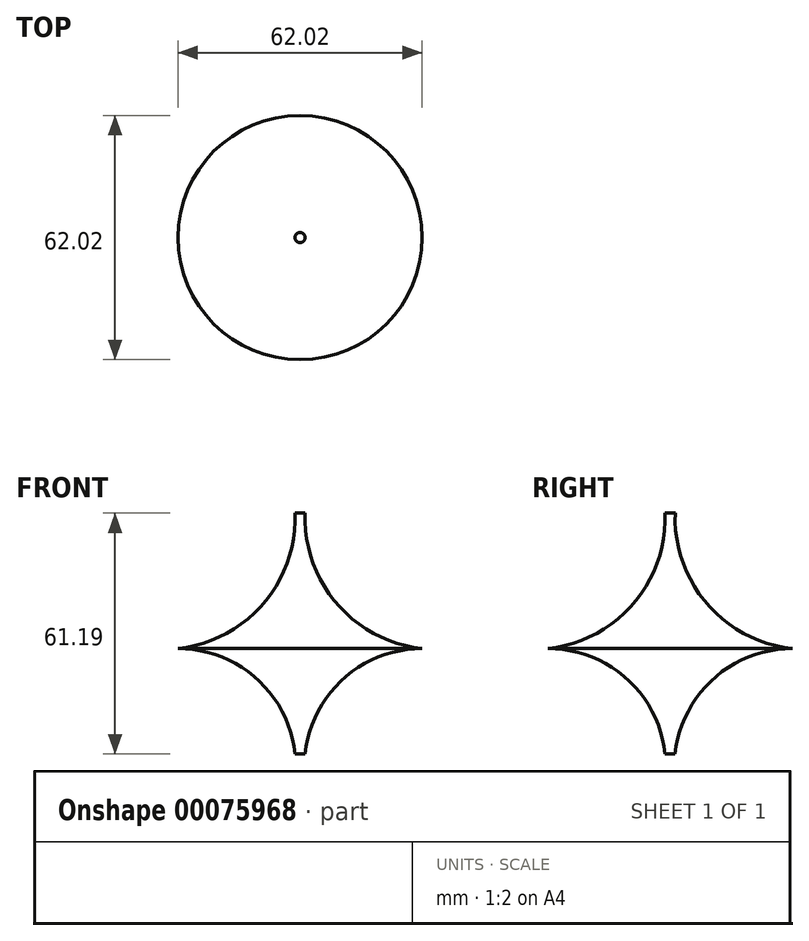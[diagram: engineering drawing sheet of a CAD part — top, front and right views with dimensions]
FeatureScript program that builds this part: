
annotation { "Feature Type Name" : "Feature", "Feature Type Description" : "" }
export const myFeature = defineFeature(function(context is Context, id is Id, definition is map)
    precondition{}
    {
        {
            var Q0;
            Q0=qCreatedBy(makeId("Front.planeOp"),FACE);
            var sketch = newSketch(context, id + "F0", { "sketchPlane" : qUnion([Q0])});
            skLineSegment(sketch, "E0", {"start": v(0, -26.8) * mm, "end": v(0, 34.4) * mm});
            skLineSegment(sketch, "E1", {"start": v(0, 34.4) * mm, "end": v(-1.3, 34.4) * mm});
            skLineSegment(sketch, "E2", {"start": v(0, -26.8) * mm, "end": v(-1.28, -26.8) * mm});
            skLineSegment(sketch, "E3", {"start": v(0, 0) * mm, "end": v(-31.01, 0) * mm});
            skArc(sketch, "E4", {"start": v(-31.01, 0) * mm, "mid": v(-9.37, 11.34) * mm, "end": v(-1.3, 34.4) * mm});
            skArc(sketch, "E5", {"start": v(-1.28, -26.8) * mm, "mid": v(-11, -7.69) * mm, "end": v(-31.01, 0) * mm});
            skSolve(sketch);
        }
        {
            var Q0;
            Q0 = qSketchRegion(id + "F0", true);
            var Q1;
            Q1=sQuery(id+"F0.wireOp",EDGE,"E0");
            revolve(context, id + "F1", {"entities" : qUnion([Q0]), "axis" : qUnion([Q1]), "revolveType" : RevolveType.FULL});
        }
    });
